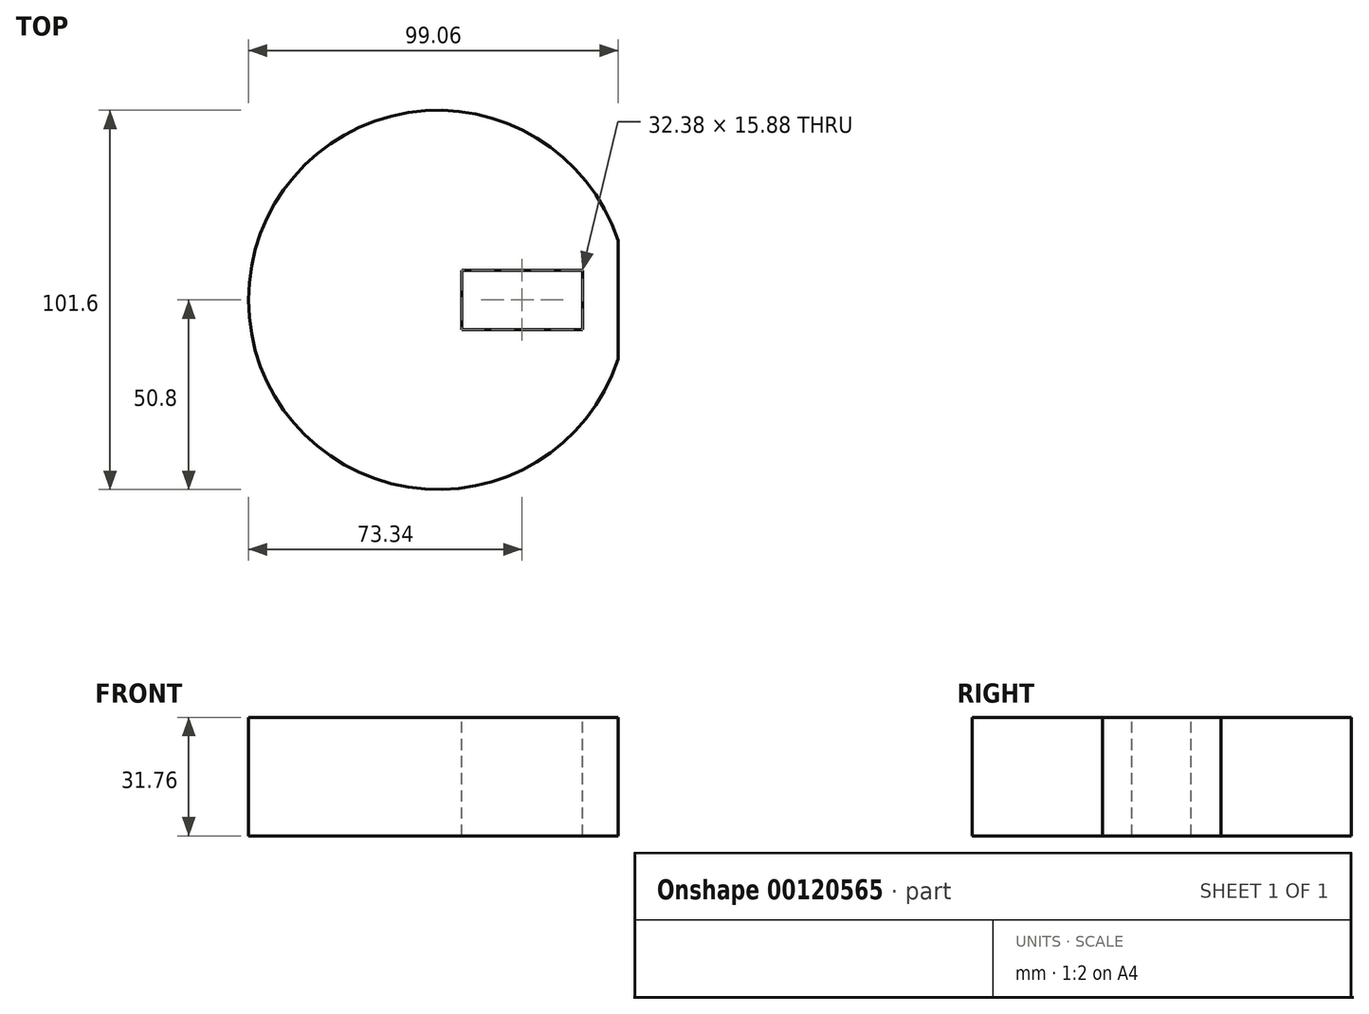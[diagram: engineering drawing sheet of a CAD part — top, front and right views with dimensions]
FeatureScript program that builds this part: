
annotation { "Feature Type Name" : "Feature", "Feature Type Description" : "" }
export const myFeature = defineFeature(function(context is Context, id is Id, definition is map)
    precondition{}
    {
        {
            var Q0;
            Q0=qCreatedBy(makeId("Top.planeOp"),FACE);
            var sketch = newSketch(context, id + "F0", { "sketchPlane" : qUnion([Q0])});
            skCircle(sketch, "E0", {"center": v(0, 0) * mm, "radius": 50.8 * mm});
            skSolve(sketch);
        }
        {
            var Q0;
            Q0 = qSketchRegion(id + "F0", true);
            extrude(context, id + "F1", {"entities" : qUnion([Q0]), "endBound" : BoundingType.SYMMETRIC, "depth" : 31.75 * mm});
        }
        {
            var Q0;
            Q0=makeQuery(id+"F1.opExtrude","CAP_FACE",FACE,{"disambiguationData":[OSD([sQuery(id+"F0.wireOp",EDGE,"E0")])],"isStart":false});
            var sketch = newSketch(context, id + "F2", { "sketchPlane" : qUnion([Q0])});
            skLineSegment(sketch, "E1.bottom", {"start": v(48.26, 15.88) * mm, "end": v(50.8, 15.88) * mm});
            skLineSegment(sketch, "E1.top", {"start": v(48.26, -15.88) * mm, "end": v(50.8, -15.88) * mm});
            skLineSegment(sketch, "E1.left", {"start": v(48.26, 15.88) * mm, "end": v(48.26, -15.88) * mm});
            skLineSegment(sketch, "E1.right", {"start": v(50.8, 15.88) * mm, "end": v(50.8, -15.88) * mm});
            skLineSegment(sketch, "E2", {"start": v(48.26, 0) * mm, "end": v(0, 0) * mm, "construction": true});
            skSolve(sketch);
        }
        {
            var Q0;
            Q0 = qSketchRegion(id + "F2", true);
            extrude(context, id + "F3", {"entities" : qUnion([Q0]), "operationType" : NewBodyOperationType.REMOVE, "endBound" : BoundingType.UP_TO_NEXT, "oppositeDirection" : true, "depth" : 25.4 * mm});
        }
        {
            var Q0;
            Q0=makeQuery(id+"F1.opExtrude","CAP_FACE",FACE,{"disambiguationData":[OSD([sQuery(id+"F0.wireOp",EDGE,"E0")])],"isStart":false});
            var sketch = newSketch(context, id + "F4", { "sketchPlane" : qUnion([Q0])});
            skLineSegment(sketch, "E3.bottom", {"start": v(38.73, 7.94) * mm, "end": v(6.35, 7.94) * mm});
            skLineSegment(sketch, "E3.top", {"start": v(38.73, -7.94) * mm, "end": v(6.35, -7.94) * mm});
            skLineSegment(sketch, "E3.left", {"start": v(38.73, 7.94) * mm, "end": v(38.73, -7.94) * mm});
            skLineSegment(sketch, "E3.right", {"start": v(6.35, 7.94) * mm, "end": v(6.35, -7.94) * mm});
            skPoint(sketch, "E3.middle", {"position": v(22.54, 0) * mm});
            skSolve(sketch);
        }
        {
            var Q0;
            Q0 = qSketchRegion(id + "F4", true);
            extrude(context, id + "F5", {"entities" : qUnion([Q0]), "operationType" : NewBodyOperationType.REMOVE, "endBound" : BoundingType.UP_TO_NEXT, "oppositeDirection" : true, "depth" : 25.4 * mm});
        }
    });
